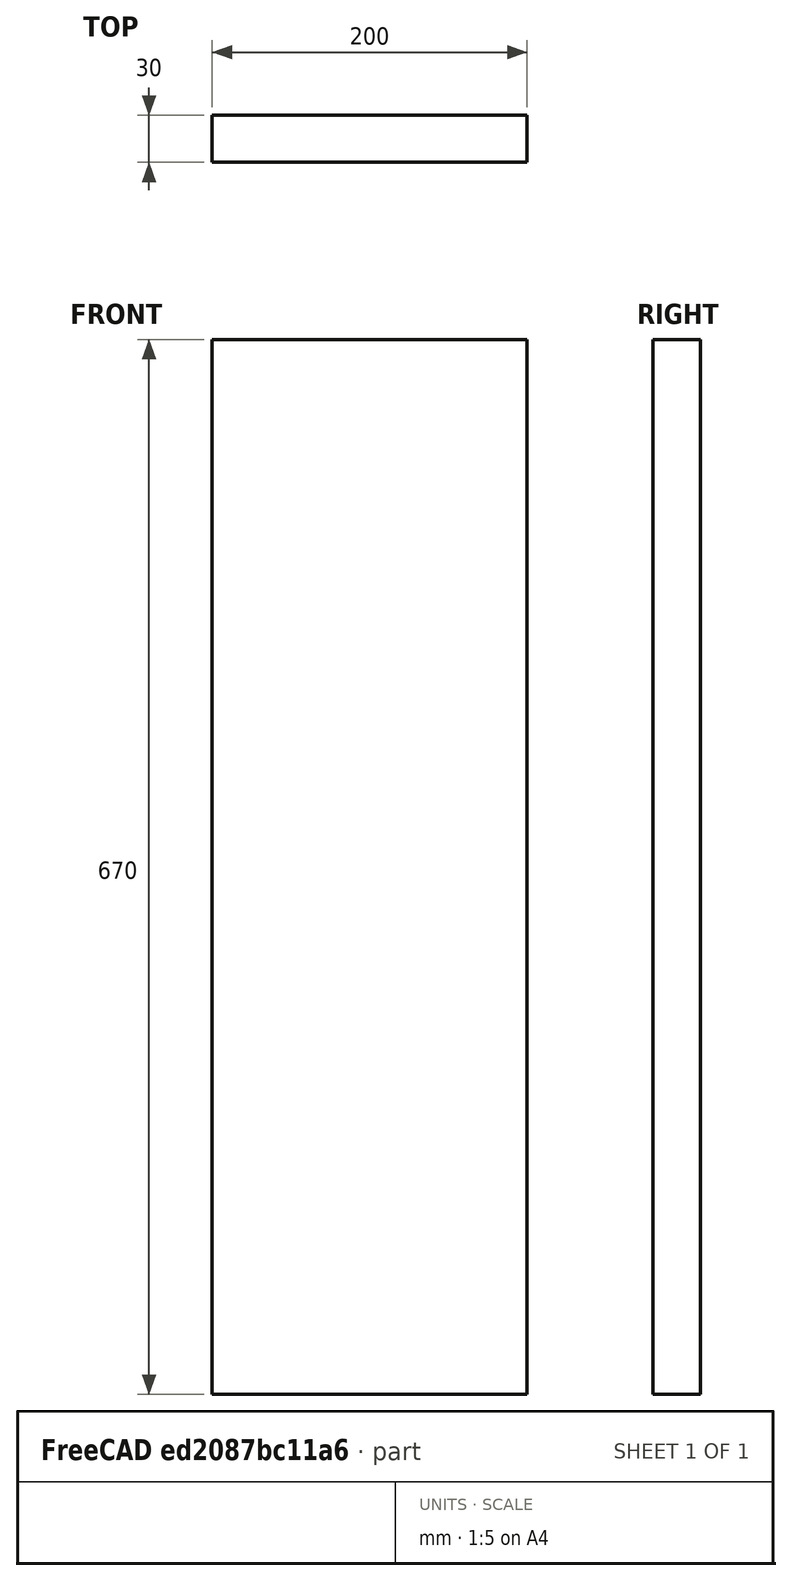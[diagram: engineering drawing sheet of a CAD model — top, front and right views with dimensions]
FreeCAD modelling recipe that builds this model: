
FCSTD DOCUMENT  (FreeCAD 1.0R39319 (Git))
Label: head-plate
License: All rights reserved
LicenseURL: https://en.wikipedia.org/wiki/All_rights_reserved
objects: Sketcher::SketchObject×1, PartDesign::Pad×1, PartDesign::Body×1
note: 6 computed .brp shape members not serialized (recipe doc carries the construction recipe); baked Part::Feature solids carry a one-line shape summary decoded from their .brp

FEATURE [Sketcher::SketchObject] Sketch
  ArcFitTolerance = 1e-06
  AttachmentSupport = -> [XZ_Plane]
  FullyConstrained = true
  MakeInternals = false
  MapMode = 5
  Placement = pos=(0,0,0) rot=(1,0,0;1.5708rad)
  sketch-geometry (4):
    g0: LineSegment StartX=0 StartY=0 StartZ=0 EndX=200 EndY=0 EndZ=0
    g1: LineSegment StartX=200 StartY=0 StartZ=0 EndX=200 EndY=670 EndZ=0
    g2: LineSegment StartX=200 StartY=670 StartZ=0 EndX=0 EndY=670 EndZ=0
    g3: LineSegment StartX=0 StartY=670 StartZ=0 EndX=0 EndY=0 EndZ=0
  constraints (11):
    c: Coincident(g0,g1)
    c: Coincident(g1,g2)
    c: Coincident(g2,g3)
    c: Coincident(g3,g0)
    c: Horizontal(g0)
    c: Horizontal(g2)
    c: Vertical(g1)
    c: Vertical(g3)
    c: Distance(g1,g3) = 200
    c: Distance(g0,g2) = 670
    c: Coincident(g0,g-1)
FEATURE [PartDesign::Pad] Pad
  Direction = (0,-1,2e-16)
  Length = 30
  Length2 = 10
  Placement = pos=(0,0,0) rot=(1,0,0;1.5708rad)
  Profile = -> Sketch
  ReferenceAxis = -> Sketch [N_Axis]
  Refine = true
  Suppressed = false
  Type = 0
FEATURE [PartDesign::Body] Body
  AllowCompound = false
  Group = -> [Sketch,Pad]
  Origin = -> Origin
  Tip = -> Pad
